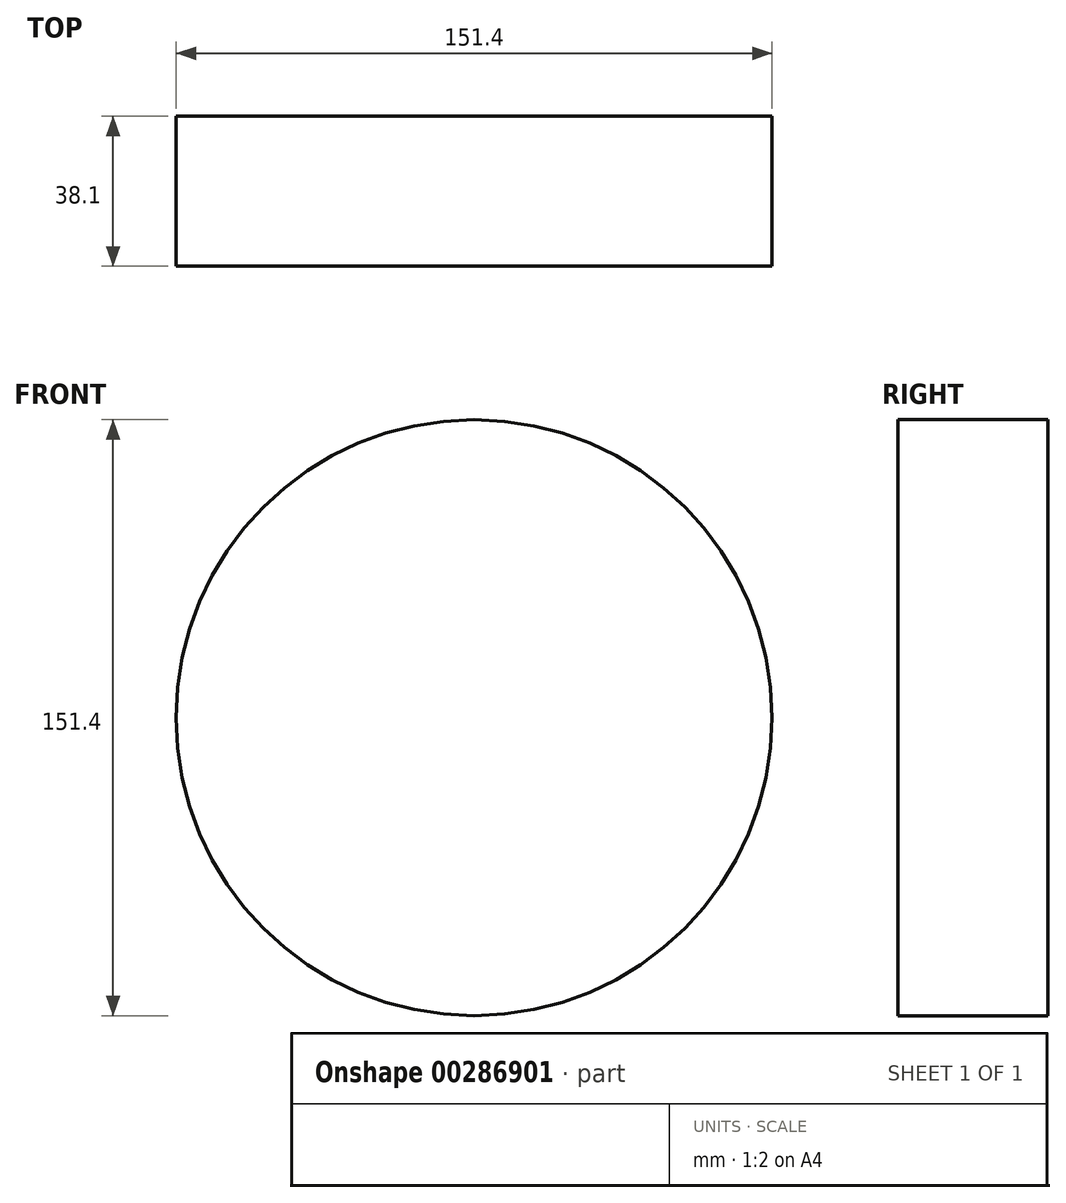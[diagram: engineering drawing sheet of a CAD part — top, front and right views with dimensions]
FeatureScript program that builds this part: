
annotation { "Feature Type Name" : "Feature", "Feature Type Description" : "" }
export const myFeature = defineFeature(function(context is Context, id is Id, definition is map)
    precondition{}
    {
        {
            var Q0;
            Q0=qCreatedBy(makeId("Front.planeOp"),FACE);
            var sketch = newSketch(context, id + "F0", { "sketchPlane" : qUnion([Q0])});
            skCircle(sketch, "E0", {"center": v(0, 0) * mm, "radius": 75.7 * mm});
            skSolve(sketch);
        }
        {
            var Q0;
            Q0 = qSketchRegion(id + "F0", true);
            extrude(context, id + "F1", {"entities" : qUnion([Q0]), "depth" : 38.1 * mm});
        }
    });
